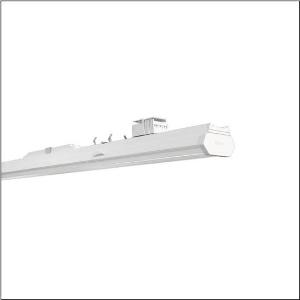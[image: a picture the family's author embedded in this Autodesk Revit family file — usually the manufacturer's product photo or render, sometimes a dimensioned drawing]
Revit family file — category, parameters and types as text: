
# Revit family: licross_11_protected_mo_51td1bmn49xg
name_source: partatom
category: Lighting Fixtures
units: mm (PartAtom-declared; Revit-internal decimal feet)

## family parameters
Cut with Voids When Loaded = No
Host = Face
Light Source = No
Part Type = Normal
Room Calculation Point = No
Round Connector Dimension = Use Diameter
Shared = No

## types (1)
- --- (1 x LED, 9410 lm, 55.3 W, 4000K)
    Apparent Load = 55 VA
    CIE Flux Codes = 54 82 95 97 100
    Color Rendering = 80
    Color Temperature = 4000K
    Default Elevation = 1800 mm
    Description = Licross 11 Protected MO, luminaire insert, of sheet steel, galvanised, coil coated, white, length: 1.500mm, width: 90mm, height: 101mm, LED rated luminous flux: 9.420lm, light colour: 840, SDCM (Standard Deviation of Colour Matching)MacAdam ≤ 2 SDCM (initial), control gear: ON/OFF Multilumen, with plug, 3-pole, with phase selection, mains connection: 220..240V, AC, 50/60Hz, rated input power: 55W, internal wiring halogen-free, primary optical cover: cover, of PMMA, light emission: direct distribution, primary light characteristic: symmetric, protection rating (complete): IP54, insulation class (complete): insulation class I (protective earthing), certification: CE, ENEC, VDE, UKCA, protection symbol: D if used in an environment with non-conductive dust loads with corresponding accessories, impact resistance: IK06, permissible ambient temperature for indoor applications: -35..+40°C, corresponds to IFS (International Featured Standards) requirements for safety and quality in the food industry, reducing of maximum allowable ambient temperature of 5°C with ceiling mounting, LABS conformity tested according to VDMA 24364:2018-05, The light source and the operating device comply with the requirements of the Ecodesign Regulation (EU) 2019/2020 and are replaceable in accordance with this regulation, packaging unit: 1 piece
    Height = 92 mm
    Lamp = 1 x LED
    Lamp Light Flux = 9410 lm
    Lamp Power = 55.3 W
    Lamp count = 1
    Length = 1500 mm
    Luminous efficacy = 170 lm/W
    Manufacturer = Siteco
    ModVariant = No
    Model = 51TD1BMN49XG
    Mounting Place = Ceiling
    Mounting Type = Pendant
    Number of Poles = 1
    OnlyDefault = Yes
    Power Factor = 1
    Product Name = Licross 11 Protected MO
    Product group = luminaire insert | ceiling pendant
    ProductGroupID = 901
    Protection Class = Protection class I
    Protection Degree = IP 54
    RLX_Detail_Level = 1
    RLX_Emergency_Light_Flux = 0 lm
    RLX_Emergency_Type = 0
    RLX_Emergency_Type_DB = No
    RlxData = <blob elided: 22253 chars, md5=77a88b93>
    Socket = socket
    Standby Power = 0 W
    System Light Flux = 9410 lm
    System Power = 55 W
    Type Comments = factory setting: luminous flux: 100 % | (A | C | E) | 126 mA
    Type Image = l_1256145.jpg
    URL = http://relux.com
    VarID = @adj_092079
    Voltage = 0 V
    Weight = 0.00 kg
    Width = 88 mm

## geometry (parser evidence)
native form markers: Blend x4, Sweep x11
no freeform markers — native parametric forms only
